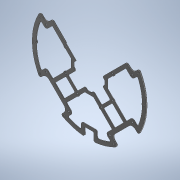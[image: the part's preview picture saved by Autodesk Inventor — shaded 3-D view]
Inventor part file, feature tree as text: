
AUTODESK INVENTOR PART (.ipt)
format: ipt  version: 2020 (Build 240168000, 168)  size: 1,584,128 bytes
history: native  units: mm
features: sketch x4, other x3, extrude x3, projected_geometry x3, fillet x2, chamfer x1
ambient origin geometry x8: Origin, YZ Plane, XZ Plane, XY Plane, X Axis, Y Axis, Z Axis, Center Point
bodies: Body1 (feature_tree)
feature tree (16):
  other  "Твердое тело1"
  other  "РабПлоскость2"
  sketch  "Эскиз1"
  other  "РабПлоскость1"
  sketch  "Эскиз3"
  extrude  "Выдавливание2"  Depth=0.5mm
  extrude  "Выдавливание3"  Depth=2.0mm TaperAngle=0.0deg
  fillet  "Сопряжение3"  Radius=1.2mm
  fillet  "Сопряжение4"  Radius=3.0mm
  extrude  "Выдавливание4"  Depth=3.0mm
  chamfer  "Фаска2"  Distance=2.0mm
  projected_geometry  "Спроецированная петля1"
  projected_geometry  "Спроецированная петля2"
  sketch  "Эскиз4"
  projected_geometry  "Спроецированная петля3"
  sketch  "Эскиз5"
